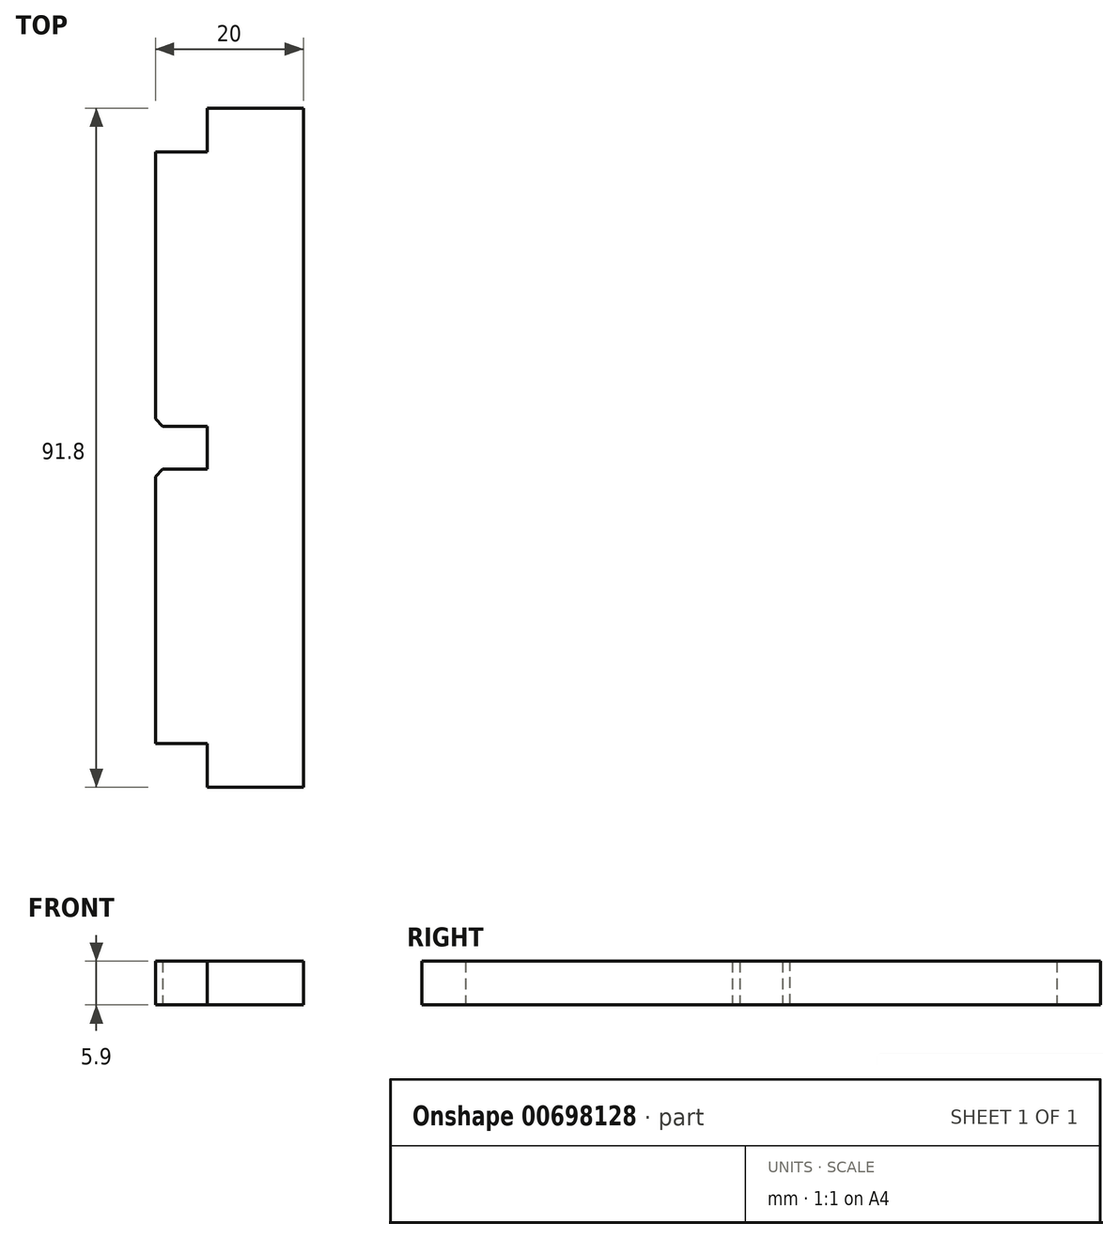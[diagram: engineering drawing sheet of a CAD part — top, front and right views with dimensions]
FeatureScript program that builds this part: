
annotation { "Feature Type Name" : "Feature", "Feature Type Description" : "" }
export const myFeature = defineFeature(function(context is Context, id is Id, definition is map)
    precondition{}
    {
        {
            assignVariable(context, id + "F0", {"name" : "wood", "anyValue" : 5.9 * mm});
        }
        {
            var Q0;
            Q0=qCreatedBy(makeId("Top.planeOp"),FACE);
            var sketch = newSketch(context, id + "F1", { "sketchPlane" : qUnion([Q0])});
            skLineSegment(sketch, "E0.bottom", {"start": v(11.67, -54.06) * mm, "end": v(4.67, -54.06) * mm});
            skLineSegment(sketch, "E0.top", {"start": v(11.67, 25.94) * mm, "end": v(4.67, 25.94) * mm});
            skLineSegment(sketch, "E0.left", {"start": v(24.67, -54.06) * mm, "end": v(24.67, 25.94) * mm});
            skLineSegment(sketch, "E0.right", {"start": v(4.67, -54.06) * mm, "end": v(4.67, -16.96) * mm});
            skPoint(sketch, "E0.middle", {"position": v(14.67, -14.06) * mm});
            skPoint(sketch, "E1", {"position": v(4.67, -14.06) * mm});
            skLineSegment(sketch, "E2.bottom", {"start": v(11.67, -16.96) * mm, "end": v(4.67, -16.96) * mm});
            skLineSegment(sketch, "E2.top", {"start": v(11.67, -11.16) * mm, "end": v(4.67, -11.16) * mm});
            skLineSegment(sketch, "E2.left", {"start": v(11.67, -16.96) * mm, "end": v(11.67, -11.16) * mm});
            skLineSegment(sketch, "E3.bottom", {"start": v(11.67, 31.84) * mm, "end": v(24.67, 31.84) * mm});
            skLineSegment(sketch, "E3.left", {"start": v(11.67, 31.84) * mm, "end": v(11.67, 25.94) * mm});
            skLineSegment(sketch, "E3.right", {"start": v(24.67, 31.84) * mm, "end": v(24.67, 25.94) * mm});
            skLineSegment(sketch, "E4", {"start": v(14.67, -14.06) * mm, "end": v(-23.36, -14.06) * mm, "construction": true});
            skLineSegment(sketch, "E5.MirrorCS", {"start": v(11.67, -59.96) * mm, "end": v(24.67, -59.96) * mm});
            skLineSegment(sketch, "E6.MirrorCS", {"start": v(11.67, -59.96) * mm, "end": v(11.67, -54.06) * mm});
            skLineSegment(sketch, "E7.MirrorCS", {"start": v(24.67, -59.96) * mm, "end": v(24.67, -54.06) * mm});
            skPoint(sketch, "E8", {"position": v(4.67, -11.16) * mm});
            skPoint(sketch, "E9", {"position": v(4.67, -16.96) * mm});
            skPoint(sketch, "E10.orphan", {"position": v(-2.33, -11.16) * mm});
            skPoint(sketch, "E11.orphan", {"position": v(-2.33, -16.96) * mm});
            skLineSegment(sketch, "E12.trimOffspring", {"start": v(4.67, -11.16) * mm, "end": v(4.67, 25.94) * mm});
            skSolve(sketch);
        }
        {
            var Q0;
            Q0=makeQuery(id+"F1.imprint","IMPRINT",FACE,{"disambiguationData":[TD([[makeQuery(id+"F1.imprint","IMPRINT",EDGE,{"derivedFrom":sQuery(id+"F1.wireOp",EDGE,"E0.bottom")}),-1.0]])]});
            extrude(context, id + "F2", {"entities" : qUnion([Q0]), "depth" : getVariable(context, 'wood'), "offsetDistance" : 25 * mm});
        }
        {
            var Q0;
            Q0=makeQuery(id+"F2.opExtrude","SWEPT_EDGE",EDGE,{"disambiguationData":[OSD([sQuery(id+"F1.wireOp",EDGE,"E2.top"),sQuery(id+"F1.wireOp",EDGE,"E12.trimOffspring")])]});
            var Q1;
            Q1=makeQuery(id+"F2.opExtrude","SWEPT_EDGE",EDGE,{"disambiguationData":[OSD([sQuery(id+"F1.wireOp",EDGE,"E0.right"),sQuery(id+"F1.wireOp",EDGE,"E2.bottom")])]});
            chamfer(context, id + "F3", {"entities" : qUnion([Q0, Q1]), "width" : 1 * mm, "tangentPropagation" : true});
        }
    });
